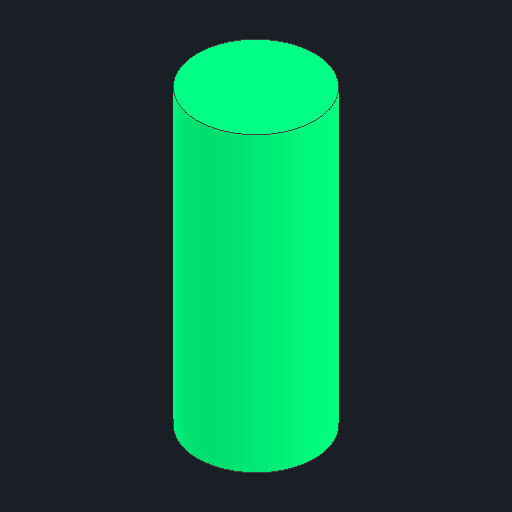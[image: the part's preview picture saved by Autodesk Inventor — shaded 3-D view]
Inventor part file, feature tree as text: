
AUTODESK INVENTOR PART (.ipt)
format: ipt  version: 2025.2 (Build 292293000, 293)  size: 83,968 bytes
history: native  units: in
note: dims shown in document units (in); Inventor stores cm internally (conversion verified against a paired STEP export)
features: other x3, sketch x1
ambient origin geometry x8: Origin, YZ Plane, XZ Plane, XY Plane, X Axis, Y Axis, Z Axis, Center Point
bodies: Solid1 (feature_tree)
feature tree (4):
  other  "26650(Green)_MIR.ipt"
  other  "Solid1::26650(Green)_MIR.ipt"
  other  "TaggingFeature1"
  sketch  "Sketch1"  dims[d0=0.3937in]
